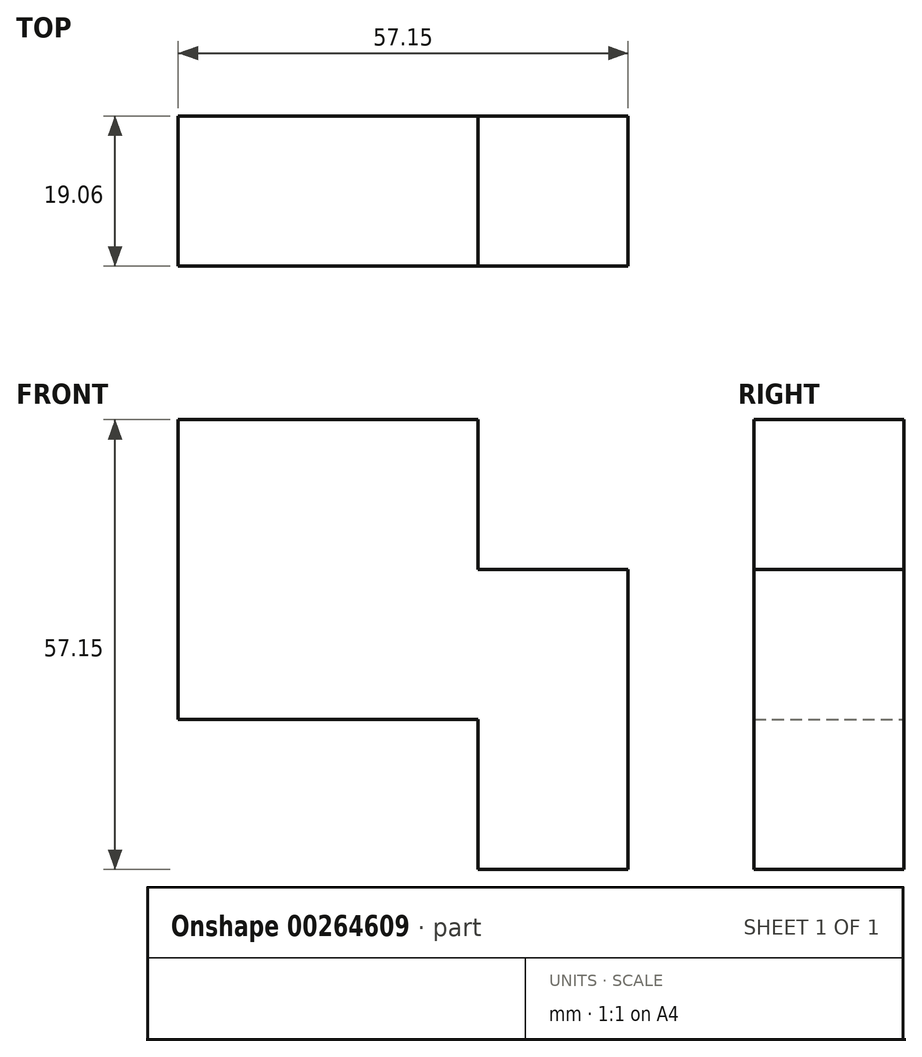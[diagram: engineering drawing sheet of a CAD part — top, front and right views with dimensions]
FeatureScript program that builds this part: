
annotation { "Feature Type Name" : "Feature", "Feature Type Description" : "" }
export const myFeature = defineFeature(function(context is Context, id is Id, definition is map)
    precondition{}
    {
        {
            var Q0;
            Q0=qCreatedBy(makeId("Front.planeOp"),FACE);
            var sketch = newSketch(context, id + "F0", { "sketchPlane" : qUnion([Q0])});
            skLineSegment(sketch, "E0.top", {"start": v(9.22, -9.83) * mm, "end": v(-9.83, -9.83) * mm});
            skLineSegment(sketch, "E0.left", {"start": v(9.22, 9.22) * mm, "end": v(9.22, -9.83) * mm});
            skLineSegment(sketch, "E0.right", {"start": v(-9.83, 9.22) * mm, "end": v(-9.83, -9.83) * mm});
            skLineSegment(sketch, "E1.top", {"start": v(9.22, 9.22) * mm, "end": v(-9.83, 9.22) * mm});
            skLineSegment(sketch, "E2.top", {"start": v(28.27, -9.83) * mm, "end": v(9.22, -9.83) * mm});
            skLineSegment(sketch, "E2.left", {"start": v(28.27, 9.22) * mm, "end": v(28.27, -9.83) * mm});
            skLineSegment(sketch, "E3.top", {"start": v(28.27, 9.22) * mm, "end": v(9.22, 9.22) * mm});
            skLineSegment(sketch, "E4.top", {"start": v(9.22, -9.83) * mm, "end": v(28.27, -9.83) * mm});
            skLineSegment(sketch, "E4.left", {"start": v(9.22, -28.88) * mm, "end": v(9.22, -9.83) * mm});
            skLineSegment(sketch, "E4.right", {"start": v(28.27, -28.88) * mm, "end": v(28.27, -9.83) * mm});
            skLineSegment(sketch, "E5.top", {"start": v(9.22, -28.88) * mm, "end": v(28.27, -28.88) * mm});
            skLineSegment(sketch, "E6.left", {"start": v(-28.88, 9.22) * mm, "end": v(-9.83, 9.22) * mm});
            skLineSegment(sketch, "E6.right", {"start": v(-28.88, -9.83) * mm, "end": v(-9.83, -9.83) * mm});
            skLineSegment(sketch, "E7.top", {"start": v(-28.88, 9.22) * mm, "end": v(-28.88, -9.83) * mm});
            skLineSegment(sketch, "E8.left", {"start": v(9.22, 28.27) * mm, "end": v(9.22, 9.22) * mm});
            skLineSegment(sketch, "E8.right", {"start": v(-9.83, 28.27) * mm, "end": v(-9.83, 9.22) * mm});
            skLineSegment(sketch, "E9.top", {"start": v(9.22, 28.27) * mm, "end": v(-9.83, 28.27) * mm});
            skLineSegment(sketch, "E10.top", {"start": v(-9.83, 9.22) * mm, "end": v(-28.88, 9.22) * mm});
            skLineSegment(sketch, "E10.right", {"start": v(-28.88, 28.27) * mm, "end": v(-28.88, 9.22) * mm});
            skLineSegment(sketch, "E11.top", {"start": v(-9.83, 28.27) * mm, "end": v(-28.88, 28.27) * mm});
            skSolve(sketch);
        }
        {
            var Q0;
            Q0 = qSketchRegion(id + "F0", true);
            extrude(context, id + "F1", {"entities" : qUnion([Q0]), "endBound" : BoundingType.SYMMETRIC, "depth" : 19.05 * mm});
        }
    });
